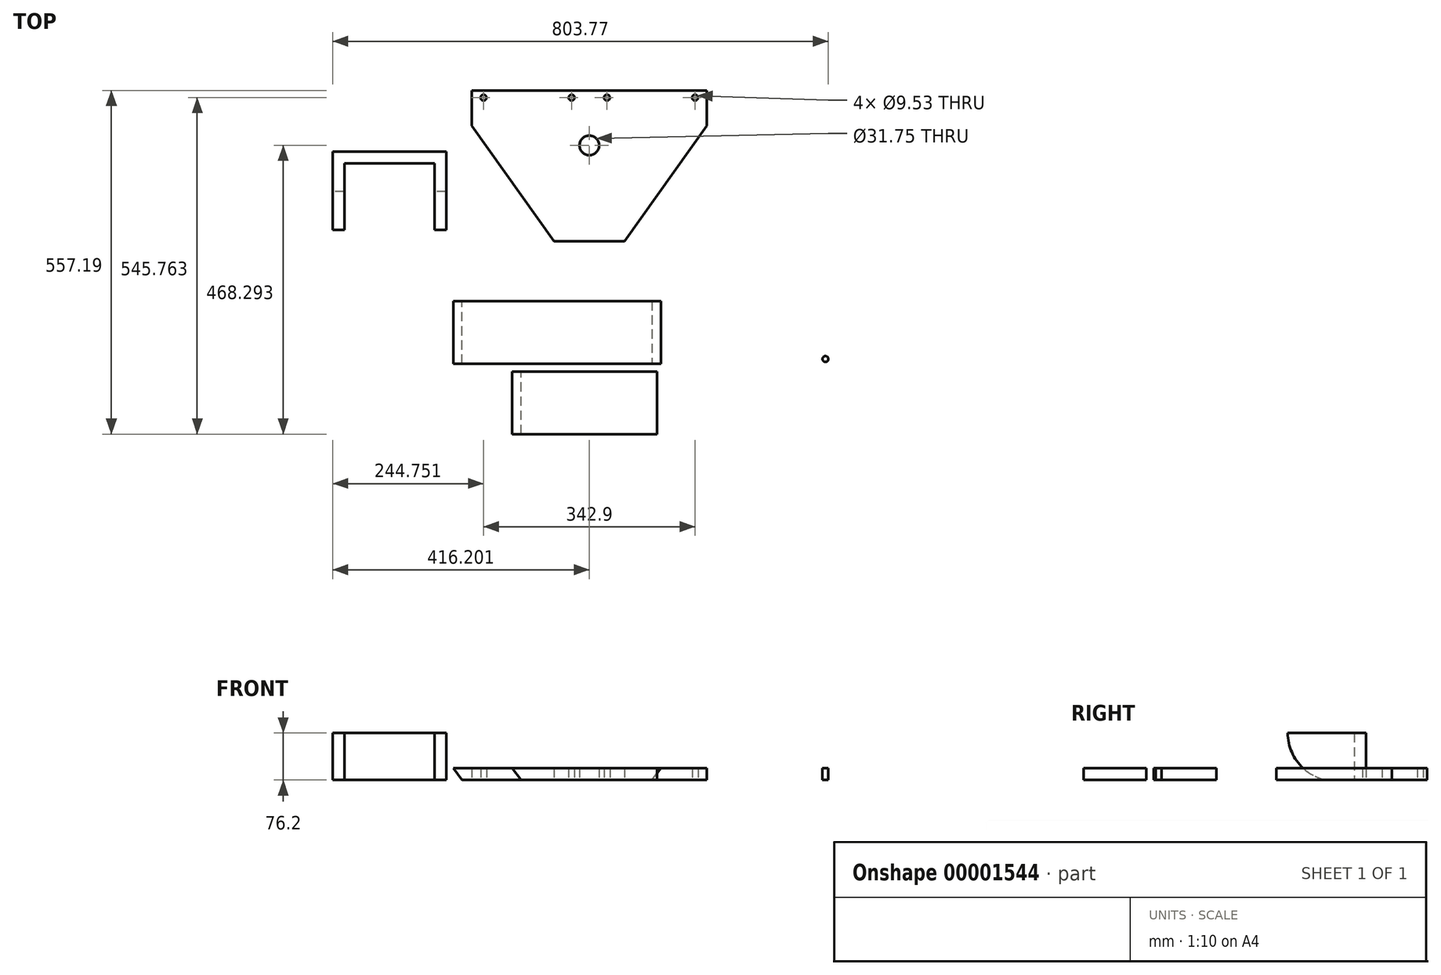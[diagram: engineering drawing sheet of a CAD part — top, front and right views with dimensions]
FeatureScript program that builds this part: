
annotation { "Feature Type Name" : "Feature", "Feature Type Description" : "" }
export const myFeature = defineFeature(function(context is Context, id is Id, definition is map)
    precondition{}
    {
        {
            var Q0;
            Q0=qCreatedBy(makeId("Top.planeOp"),FACE);
            var sketch = newSketch(context, id + "F0", { "sketchPlane" : qUnion([Q0])});
            skLineSegment(sketch, "E0", {"start": v(-181.4, 47.7) * mm, "end": v(155.14, 47.7) * mm});
            skLineSegment(sketch, "E1", {"start": v(155.14, 47.7) * mm, "end": v(155.14, -53.9) * mm});
            skLineSegment(sketch, "E2", {"start": v(155.14, -53.9) * mm, "end": v(-181.4, -53.9) * mm});
            skLineSegment(sketch, "E3", {"start": v(-181.4, 47.7) * mm, "end": v(-181.4, -53.9) * mm});
            skSolve(sketch);
        }
        {
            var Q0;
            Q0=makeQuery(id+"F0.imprint","IMPRINT",FACE,{"disambiguationData":[TD([[makeQuery(id+"F0.imprint","IMPRINT",EDGE,{"derivedFrom":sQuery(id+"F0.wireOp",EDGE,"E0")}),-1.0]])]});
            extrude(context, id + "F1", {"entities" : qUnion([Q0]), "depth" : 19.05 * mm});
        }
        {
            var Q0;
            Q0=makeQuery(id+"F1.opExtrude","CAP_EDGE",EDGE,{"disambiguationData":[OSD([sQuery(id+"F0.wireOp",EDGE,"E3")])],"isStart":true});
            var Q1;
            Q1=makeQuery(id+"F1.opExtrude","CAP_EDGE",EDGE,{"disambiguationData":[OSD([sQuery(id+"F0.wireOp",EDGE,"E1")])],"isStart":true});
            chamfer(context, id + "F2", {"entities" : qUnion([Q0, Q1]), "chamferType" : ChamferType.OFFSET_ANGLE, "width" : 19.05 * mm, "oppositeDirection" : false, "angle" : 37 * degree, "tangentPropagation" : true});
        }
        {
            var Q0;
            Q0=qCreatedBy(makeId("Top.planeOp"),FACE);
            var sketch = newSketch(context, id + "F3", { "sketchPlane" : qUnion([Q0])});
            skLineSegment(sketch, "E4.bottom", {"start": v(-85.9, -66.35) * mm, "end": v(149.05, -66.35) * mm});
            skLineSegment(sketch, "E4.top", {"start": v(-85.9, -167.95) * mm, "end": v(149.05, -167.95) * mm});
            skLineSegment(sketch, "E4.left", {"start": v(-85.9, -66.35) * mm, "end": v(-85.9, -167.95) * mm});
            skLineSegment(sketch, "E4.right", {"start": v(149.05, -66.35) * mm, "end": v(149.05, -167.95) * mm});
            skSolve(sketch);
        }
        {
            var Q0;
            Q0=makeQuery(id+"F3.imprint","IMPRINT",FACE,{"disambiguationData":[TD([[makeQuery(id+"F3.imprint","IMPRINT",EDGE,{"derivedFrom":sQuery(id+"F3.wireOp",EDGE,"E4.bottom")}),-1.0]])]});
            extrude(context, id + "F4", {"entities" : qUnion([Q0]), "depth" : 19.05 * mm});
        }
        {
            var Q0;
            Q0=makeQuery(id+"F4.opExtrude","CAP_EDGE",EDGE,{"disambiguationData":[OSD([sQuery(id+"F3.wireOp",EDGE,"E4.left")])],"isStart":true});
            chamfer(context, id + "F5", {"entities" : qUnion([Q0]), "chamferType" : ChamferType.OFFSET_ANGLE, "width" : 19.05 * mm, "oppositeDirection" : false, "angle" : 37 * degree, "tangentPropagation" : true});
        }
        {
            var Q0;
            Q0=qCreatedBy(makeId("Top.planeOp"),FACE);
            var sketch = newSketch(context, id + "F6", { "sketchPlane" : qUnion([Q0])});
            skLineSegment(sketch, "E5", {"start": v(-151.45, 389.24) * mm, "end": v(229.55, 389.24) * mm});
            skLineSegment(sketch, "E6", {"start": v(229.55, 389.24) * mm, "end": v(229.55, 332.1) * mm});
            skLineSegment(sketch, "E7", {"start": v(39.05, 389.24) * mm, "end": v(39.05, 107.56) * mm, "construction": true});
            skLineSegment(sketch, "E8", {"start": v(-151.45, 389.24) * mm, "end": v(-151.45, 332.1) * mm});
            skCircle(sketch, "E9", {"center": v(39.05, 300.34) * mm, "radius": 15.88 * mm});
            skLineSegment(sketch, "E10", {"start": v(-18.1, 144.77) * mm, "end": v(96.2, 144.77) * mm});
            skLineSegment(sketch, "E11", {"start": v(-151.45, 332.1) * mm, "end": v(-18.1, 144.77) * mm});
            skLineSegment(sketch, "E12", {"start": v(96.2, 144.77) * mm, "end": v(229.55, 332.1) * mm});
            skCircle(sketch, "E13", {"center": v(-132.4, 377.81) * mm, "radius": 4.76 * mm});
            skCircle(sketch, "E14", {"center": v(10.35, 377.81) * mm, "radius": 4.76 * mm});
            skCircle(sketch, "E15.0.MirrorC", {"center": v(210.5, 377.81) * mm, "radius": 4.76 * mm});
            skCircle(sketch, "E15.1.MirrorC", {"center": v(67.75, 377.81) * mm, "radius": 4.76 * mm});
            skSolve(sketch);
        }
        {
            var Q0;
            Q0=makeQuery(id+"F6.imprint","IMPRINT",FACE,{"disambiguationData":[TD([[makeQuery(id+"F6.imprint","IMPRINT",EDGE,{"derivedFrom":sQuery(id+"F6.wireOp",EDGE,"E5")}),-1.0]])]});
            extrude(context, id + "F7", {"entities" : qUnion([Q0]), "depth" : 19.05 * mm});
        }
        {
            var Q0;
            Q0=qCreatedBy(makeId("Top.planeOp"),FACE);
            var sketch = newSketch(context, id + "F8", { "sketchPlane" : qUnion([Q0])});
            skLineSegment(sketch, "E16.bottom", {"start": v(-377.15, 290.21) * mm, "end": v(-193, 290.21) * mm});
            skLineSegment(sketch, "E16.top", {"start": v(-358.1, 271.16) * mm, "end": v(-212.05, 271.16) * mm});
            skLineSegment(sketch, "E16.left", {"start": v(-377.15, 290.21) * mm, "end": v(-377.15, 271.16) * mm});
            skLineSegment(sketch, "E16.right", {"start": v(-193, 290.21) * mm, "end": v(-193, 271.16) * mm});
            skLineSegment(sketch, "E17.top", {"start": v(-377.15, 163.21) * mm, "end": v(-358.1, 163.21) * mm});
            skLineSegment(sketch, "E17.left", {"start": v(-377.15, 271.16) * mm, "end": v(-377.15, 163.21) * mm});
            skLineSegment(sketch, "E17.right", {"start": v(-358.1, 271.16) * mm, "end": v(-358.1, 163.21) * mm});
            skLineSegment(sketch, "E18.top", {"start": v(-193, 163.21) * mm, "end": v(-212.05, 163.21) * mm});
            skLineSegment(sketch, "E18.left", {"start": v(-193, 271.16) * mm, "end": v(-193, 163.21) * mm});
            skLineSegment(sketch, "E18.right", {"start": v(-212.05, 271.16) * mm, "end": v(-212.05, 163.21) * mm});
            skSolve(sketch);
        }
        {
            var Q0;
            Q0=makeQuery(id+"F8.imprint","IMPRINT",FACE,{"disambiguationData":[TD([[makeQuery(id+"F8.imprint","IMPRINT",EDGE,{"derivedFrom":sQuery(id+"F8.wireOp",EDGE,"E16.bottom")}),-1.0]])]});
            extrude(context, id + "F9", {"entities" : qUnion([Q0]), "depth" : 76.2 * mm});
        }
        {
            var Q0;
            Q0=makeQuery(id+"F9.opExtrude","SWEPT_FACE",FACE,{"disambiguationData":[OSD([sQuery(id+"F8.wireOp",EDGE,"E16.left")])]});
            var sketch = newSketch(context, id + "F10", { "sketchPlane" : qUnion([Q0])});
            skArc(sketch, "E19", {"start": v(-225.72, 0) * mm, "mid": v(-180.84, 26.92) * mm, "end": v(-163.21, 76.2) * mm});
            skLineSegment(sketch, "E20", {"start": v(-163.21, 76.2) * mm, "end": v(-163.21, 0) * mm});
            skLineSegment(sketch, "E21", {"start": v(-163.21, 0) * mm, "end": v(-225.72, 0) * mm});
            skSolve(sketch);
        }
        {
            var Q0;
            Q0=makeQuery(id+"F10.imprint","IMPRINT",FACE,{"disambiguationData":[TD([[makeQuery(id+"F10.imprint","IMPRINT",EDGE,{"derivedFrom":sQuery(id+"F10.wireOp",EDGE,"E19")}),-1.0]])]});
            extrude(context, id + "F11", {"entities" : qUnion([Q0]), "operationType" : NewBodyOperationType.REMOVE, "oppositeDirection" : true, "depth" : 190.5 * mm});
        }
        {
            var Q0;
            Q0=qCreatedBy(makeId("Top.planeOp"),FACE);
            var sketch = newSketch(context, id + "F12", { "sketchPlane" : qUnion([Q0])});
            skLineSegment(sketch, "E22.bottom", {"start": v(179.4, 149.93) * mm, "end": v(463.88, 149.93) * mm});
            skLineSegment(sketch, "E23", {"start": v(463.88, 149.93) * mm, "end": v(431.73, -84.44) * mm});
            skLineSegment(sketch, "E24", {"start": v(179.4, 149.93) * mm, "end": v(211.54, -84.44) * mm});
            skArc(sketch, "E25", {"start": v(211.54, -84.44) * mm, "mid": v(321.64, -180.46) * mm, "end": v(431.73, -84.44) * mm});
            skLineSegment(sketch, "E26.rect.bottom", {"start": v(321.64, -167.57) * mm, "end": v(321.64, -167.57) * mm});
            skLineSegment(sketch, "E26.rect.top", {"start": v(321.64, 111.83) * mm, "end": v(321.64, 111.83) * mm});
            skLineSegment(sketch, "E26.rect.left", {"start": v(329.9, -159.32) * mm, "end": v(329.9, 103.57) * mm});
            skLineSegment(sketch, "E26.rect.right", {"start": v(313.38, -159.32) * mm, "end": v(313.38, 103.57) * mm});
            skPoint(sketch, "E26.rect.middle", {"position": v(321.64, -27.87) * mm});
            skPoint(sketch, "E27.visualSharp", {"position": v(313.38, 111.83) * mm});
            skArc(sketch, "E27.filletArc", {"start": v(321.64, 111.83) * mm, "mid": v(315.8, 109.4) * mm, "end": v(313.38, 103.57) * mm});
            skPoint(sketch, "E28.visualSharp", {"position": v(329.9, 111.83) * mm});
            skArc(sketch, "E28.filletArc", {"start": v(329.9, 103.57) * mm, "mid": v(327.48, 109.4) * mm, "end": v(321.64, 111.83) * mm});
            skPoint(sketch, "E29.visualSharp", {"position": v(313.38, -167.57) * mm});
            skArc(sketch, "E29.filletArc", {"start": v(313.38, -159.32) * mm, "mid": v(315.8, -165.16) * mm, "end": v(321.64, -167.57) * mm});
            skPoint(sketch, "E30.visualSharp", {"position": v(329.9, -167.57) * mm});
            skArc(sketch, "E30.filletArc", {"start": v(321.64, -167.57) * mm, "mid": v(327.48, -165.16) * mm, "end": v(329.9, -159.32) * mm});
            skSolve(sketch);
        }
        {
            var Q0;
            Q0 = qSketchRegion(id + "F12", true);
            extrude(context, id + "F13", {"entities" : qUnion([Q0]), "depth" : 19.05 * mm});
        }
        {
            var Q0;
            Q0=makeQuery(id+"F13.opExtrude","CAP_FACE",FACE,{"disambiguationData":[OSD([sQuery(id+"F12.wireOp",EDGE,"E22.bottom"),sQuery(id+"F12.wireOp",EDGE,"E23"),sQuery(id+"F12.wireOp",EDGE,"E24"),sQuery(id+"F12.wireOp",EDGE,"E25"),sQuery(id+"F12.wireOp",EDGE,"E26.rect.left"),sQuery(id+"F12.wireOp",EDGE,"E26.rect.right"),sQuery(id+"F12.wireOp",EDGE,"E27.filletArc"),sQuery(id+"F12.wireOp",EDGE,"E28.filletArc"),sQuery(id+"F12.wireOp",EDGE,"E29.filletArc"),sQuery(id+"F12.wireOp",EDGE,"E30.filletArc")])],"isStart":false});
            var sketch = newSketch(context, id + "F14", { "sketchPlane" : qUnion([Q0])});
            skCircle(sketch, "E31", {"center": v(221.42, -46.16) * mm, "radius": 4.76 * mm});
            skLineSegment(sketch, "E32", {"start": v(321.64, 111.83) * mm, "end": v(321.64, -151.06) * mm, "construction": true});
            skCircle(sketch, "E33.0.MirrorC", {"center": v(421.86, -46.16) * mm, "radius": 4.76 * mm});
            skSolve(sketch);
        }
        {
            var Q0;
            {Q0=qUnion([makeQuery(id+"F14.imprint","IMPRINT",FACE,{"disambiguationData":[TD([[makeQuery(id+"F14.imprint","IMPRINT",EDGE,{"derivedFrom":sQuery(id+"F14.wireOp",EDGE,"E31")}),1.0]])]}),makeQuery(id+"F14.imprint","IMPRINT",FACE,{"disambiguationData":[TD([[makeQuery(id+"F14.imprint","IMPRINT",EDGE,{"derivedFrom":sQuery(id+"F14.wireOp",EDGE,"E33.0.MirrorC")}),-1.0]])]})]);}
            extrude(context, id + "F15", {"entities" : qUnion([Q0]), "operationType" : NewBodyOperationType.REMOVE, "endBound" : BoundingType.THROUGH_ALL, "oppositeDirection" : true, "depth" : 25.4 * mm});
        }
    });
